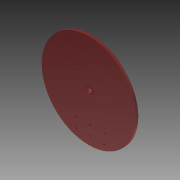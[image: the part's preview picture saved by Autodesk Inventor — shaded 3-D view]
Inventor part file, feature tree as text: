
AUTODESK INVENTOR PART (.ipt)
format: ipt  version: 2013 (Build 170138000, 138)  size: 136,704 bytes
history: native  units: mm
features: sketch x4, extrude x2, hole x2, other x1
ambient origin geometry x8: Origin, YZ Plane, XZ Plane, XY Plane, X Axis, Y Axis, Z Axis, Center Point
feature tree (9):
  other  "ソリッド1"
  extrude  "押し出し1"  Depth=200.0mm
  hole  "穴5"  [1 undecoded]
  extrude  "押し出し4"  Depth=7.0mm
  hole  "穴6"  [1 undecoded]
  sketch  "スケッチ1"
  sketch  "スケッチ12"
  sketch  "スケッチ13"
  sketch  "スケッチ14"
note: 2 required parameter values undecoded (feature->parameter linkage not recoverable at this tier; creation-order binding heuristic only, values carry confidence <= 0.55)
